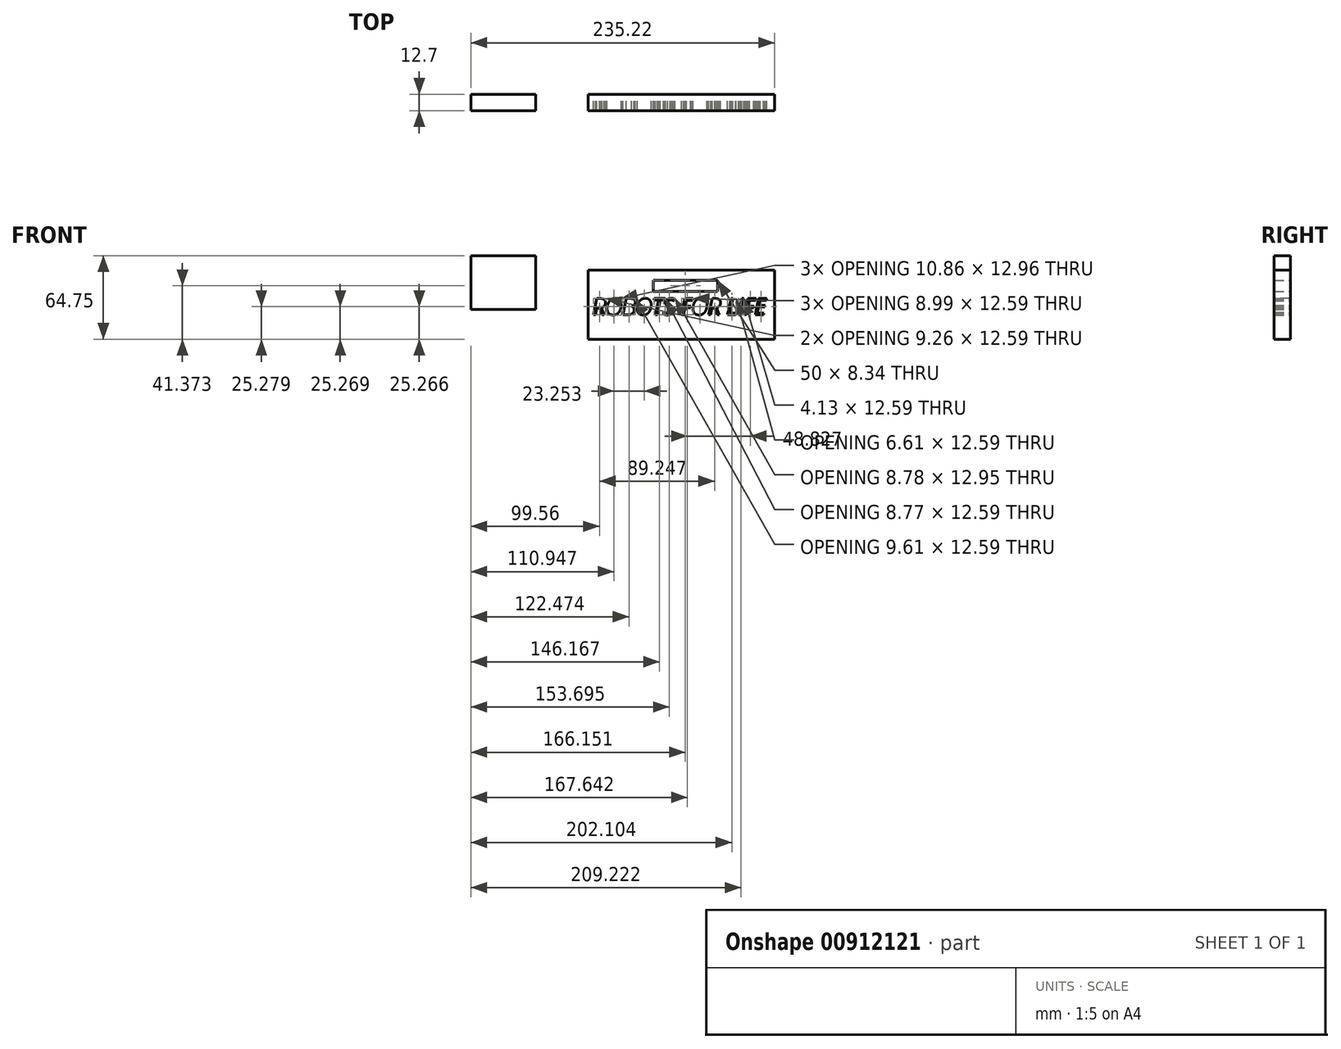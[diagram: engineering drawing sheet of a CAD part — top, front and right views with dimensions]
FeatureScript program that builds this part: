
annotation { "Feature Type Name" : "Feature", "Feature Type Description" : "" }
export const myFeature = defineFeature(function(context is Context, id is Id, definition is map)
    precondition{}
    {
        {
            var Q0;
            Q0=qCreatedBy(makeId("Front.planeOp"),FACE);
            var sketch = newSketch(context, id + "F0", { "sketchPlane" : qUnion([Q0])});
            skText(sketch, "E0", { "text": "ROBOTS FOR LIFE ", "fontName": "OpenSans-Italic.ttf"});
            skLineSegment(sketch, "E1.bottom", {"start": v(-9.97, 25.41) * mm, "end": v(134.35, 25.41) * mm});
            skLineSegment(sketch, "E1.top", {"start": v(-9.97, -28.13) * mm, "end": v(134.35, -28.13) * mm});
            skLineSegment(sketch, "E1.left", {"start": v(-9.97, 25.41) * mm, "end": v(-9.97, -28.13) * mm});
            skLineSegment(sketch, "E1.right", {"start": v(134.35, 25.41) * mm, "end": v(134.35, -28.13) * mm});
            skLineSegment(sketch, "E2.bottom", {"start": v(40.28, 17.42) * mm, "end": v(90.28, 17.42) * mm});
            skLineSegment(sketch, "E2.top", {"start": v(40.28, 9.07) * mm, "end": v(90.28, 9.07) * mm});
            skLineSegment(sketch, "E2.left", {"start": v(40.28, 17.42) * mm, "end": v(40.28, 9.07) * mm});
            skLineSegment(sketch, "E2.right", {"start": v(90.28, 17.42) * mm, "end": v(90.28, 9.07) * mm});
            skLineSegment(sketch, "E3.bottom", {"start": v(-100.87, 36.62) * mm, "end": v(-50.87, 36.62) * mm});
            skLineSegment(sketch, "E3.top", {"start": v(-100.87, -4.98) * mm, "end": v(-50.87, -4.98) * mm});
            skLineSegment(sketch, "E3.left", {"start": v(-100.87, 36.62) * mm, "end": v(-100.87, -4.98) * mm});
            skLineSegment(sketch, "E3.right", {"start": v(-50.87, 36.62) * mm, "end": v(-50.87, -4.98) * mm});
            const initialGuessF0  = {"E0": [-0.00668, -0.00916, 1, 0, 0.0127]};
            skSetInitialGuess(sketch, initialGuessF0);
            skSolve(sketch);
        }
        {
            var Q0;
            Q0=makeQuery(id+"F0.imprint","IMPRINT",FACE,{"disambiguationData":[TD([[makeQuery(id+"F0.imprint","IMPRINT",EDGE,{"derivedFrom":sQuery(id+"F0.wireOp",EDGE,"E0.sketch_text.stroke-0")}),1.0]])]});
            extrude(context, id + "F1", {"entities" : qUnion([Q0]), "depth" : 12.7 * mm, "offsetDistance" : 25.4 * mm});
        }
        {
            var Q0;
            Q0 = qSketchRegion(id + "F0", true);
            extrude(context, id + "F2", {"entities" : qUnion([Q0]), "operationType" : NewBodyOperationType.ADD, "depth" : 12.7 * mm, "offsetDistance" : 25.4 * mm});
        }
    });
